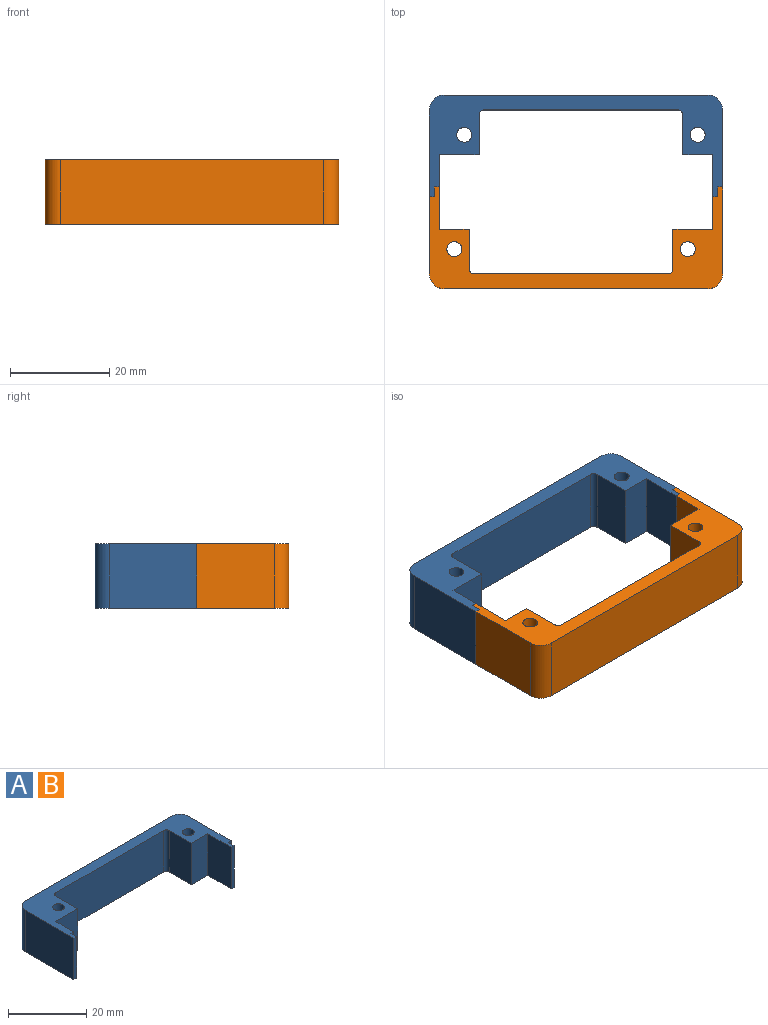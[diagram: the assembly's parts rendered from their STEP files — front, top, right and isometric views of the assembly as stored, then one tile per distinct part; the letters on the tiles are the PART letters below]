
ASSEMBLY  parts=2 mates=1
PART A: 24 faces, bbox 59x20.5x13 mm
  f0: plane 13x1mm, normal (0,-1,0), area 13mm2, adj f1,f21,f22,f23
  f1: plane 13x2mm, normal (1,0,0), area 26mm2, adj f0,f2,f22,f23
  f2: plane 13x1mm, normal (0,-1,0), area 13mm2, adj f1,f3,f22,f23
  f3: plane 15.5x13mm, normal (1,0,0), area 201.5mm2, adj f2,f4,f22,f23
  f4: cylinder r=3mm len=13mm, axis (0,0,-1), area 61.3mm2, adj f3,f5,f22,f23
  f5: plane 53x13mm, normal (0,1,0), area 689mm2, adj f4,f6,f22,f23
  f6: cylinder r=3mm len=13mm, axis (0,0,-1), area 61.3mm2, adj f5,f7,f22,f23
  f7: plane 17.5x13mm, normal (-1,0,0), area 227.5mm2, adj f6,f8,f22,f23
  f8: plane 13x1mm, normal (0,-1,0), area 13mm2, adj f7,f9,f22,f23
  f9: plane 13x2mm, normal (1,0,0), area 26mm2, adj f8,f10,f22,f23
  f10: plane 13x1mm, normal (0,-1,0), area 13mm2, adj f9,f11,f22,f23
  f11: plane 13x6.5mm, normal (1,0,0), area 84.5mm2, adj f10,f12,f22,f23
  f12: plane 13x8mm, normal (0,-1,0), area 104mm2, adj f11,f13,f22,f23
  f13: plane 13x8mm, normal (1,0,0), area 104mm2, adj f12,f14,f22,f23
  f14: cylinder r=1mm len=13mm, axis (0,0,-1), area 20.4mm2, adj f13,f15,f22,f23
  f15: plane 39x13mm, normal (0,-1,0), area 507mm2, adj f14,f16,f22,f23
  f16: cylinder r=1mm len=13mm, axis (0,0,-1), area 20.4mm2, adj f15,f17,f22,f23
  f17: plane 13x8mm, normal (-1,0,0), area 104mm2, adj f16,f18,f22,f23
  f18: plane 13x6mm, normal (0,-1,0), area 78mm2, adj f17,f21,f22,f23
  f19: cylinder r=1.5mm len=13mm, axis (0,0,-1), area 122.5mm2, adj f22,f23
  f20: cylinder r=1.5mm len=13mm, axis (0,0,-1), area 122.5mm2, adj f22,f23
  f21: plane 13x8.5mm, normal (-1,0,0), area 110.5mm2, adj f0,f18,f22,f23
  f22: plane 59x20.5mm, normal (0,0,1), area 351.4mm2, adj f0,f1,f2,f3,f4,f5,f6,f7
  f23: plane 59x20.5mm, normal (0,0,-1), area 351.4mm2, adj f0,f1,f2,f3,f4,f5,f6,f7
PART B: same geometry as A
PLACE A at identity
PLACE B rot(axis=(0,0,1),180deg) t=(-9.86,-16.01,0)mm
MATE fastened B.f8 <-> A.f2  axis (0,1,0) through (24.07,-7,13)mm
